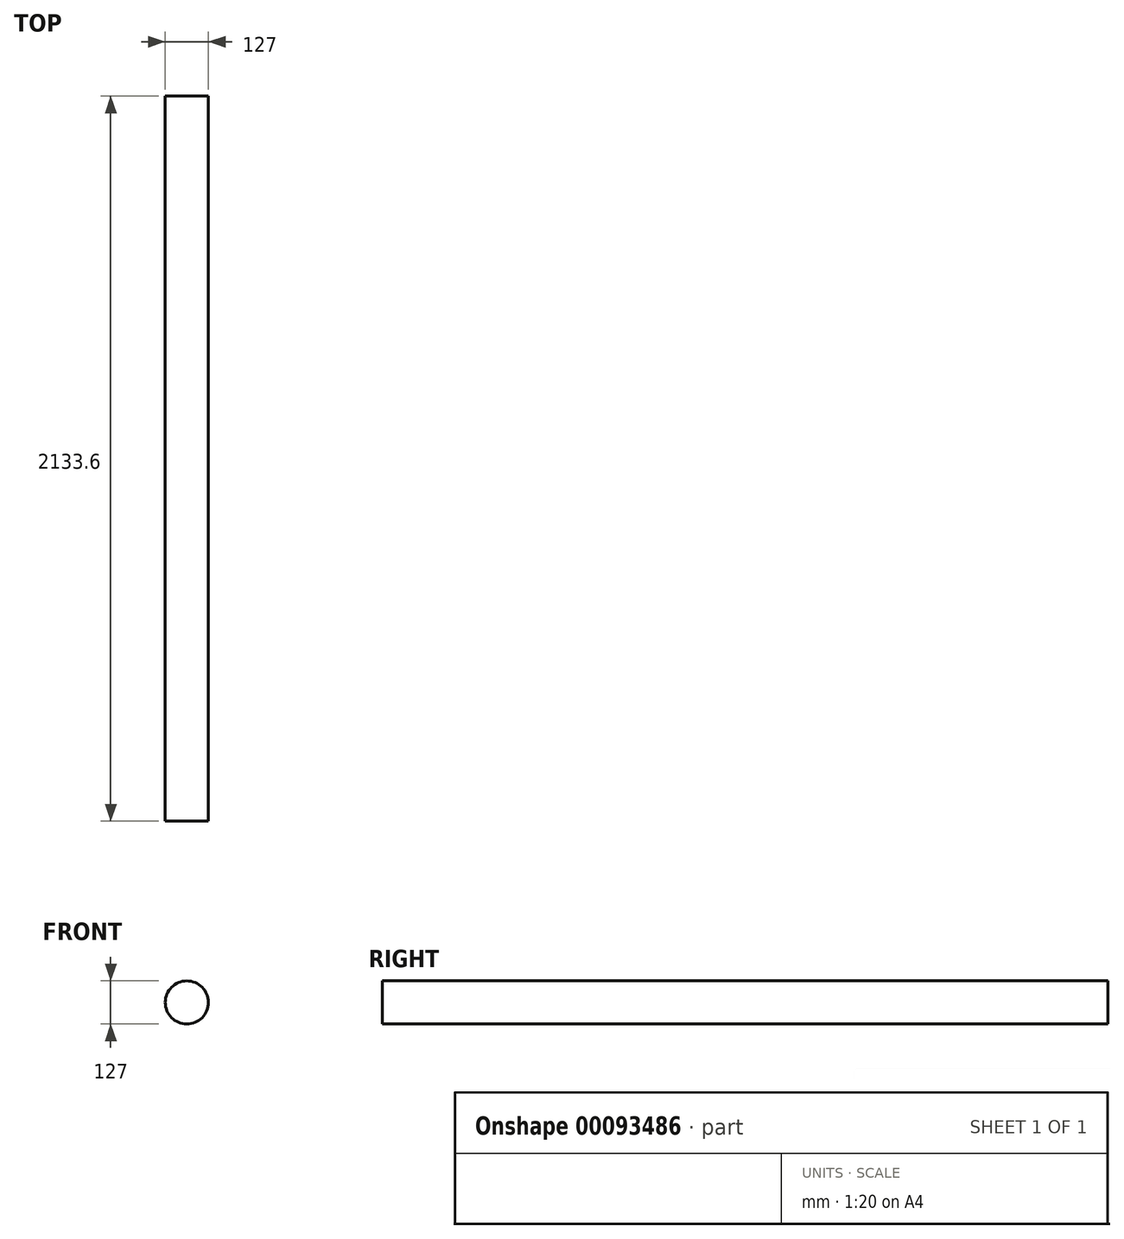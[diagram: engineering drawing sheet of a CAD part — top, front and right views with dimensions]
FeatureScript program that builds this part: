
annotation { "Feature Type Name" : "Feature", "Feature Type Description" : "" }
export const myFeature = defineFeature(function(context is Context, id is Id, definition is map)
    precondition{}
    {
        {
            var Q0;
            Q0=qCreatedBy(makeId("Front.planeOp"),FACE);
            var sketch = newSketch(context, id + "F0", { "sketchPlane" : qUnion([Q0])});
            skCircle(sketch, "E0", {"center": v(0, 0) * mm, "radius": 63.5 * mm});
            skSolve(sketch);
        }
        {
            var Q0;
            Q0=makeQuery(id+"F0.imprint","IMPRINT",FACE,{"disambiguationData":[TD([[makeQuery(id+"F0.imprint","IMPRINT",EDGE,{"derivedFrom":sQuery(id+"F0.wireOp",EDGE,"E0")}),1.0]])]});
            extrude(context, id + "F1", {"entities" : qUnion([Q0]), "depth" : 2133.6 * mm});
        }
    });
